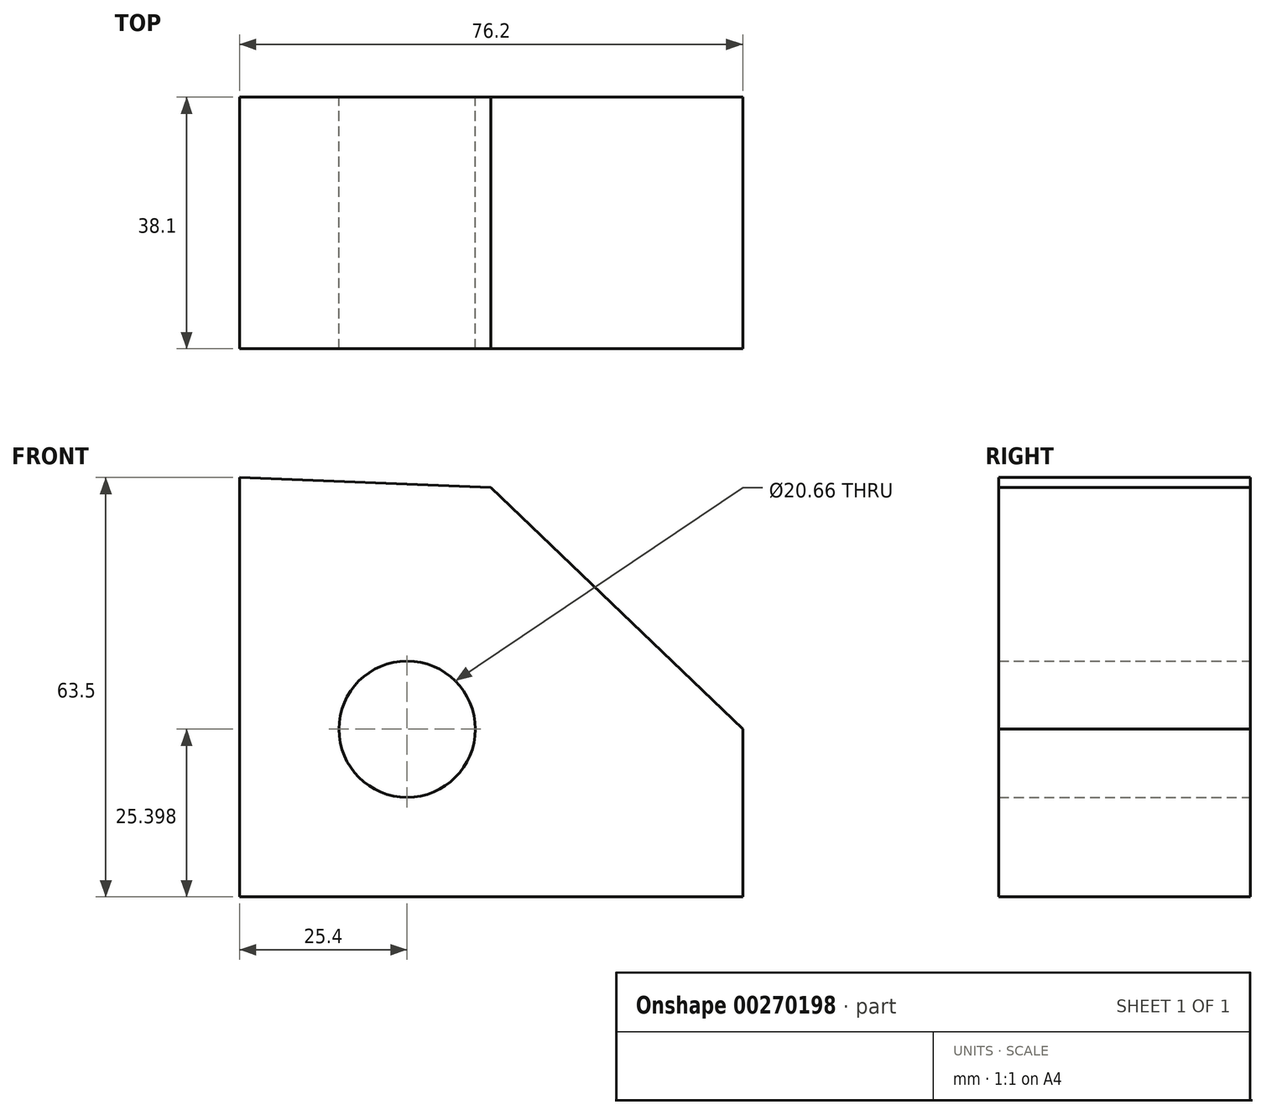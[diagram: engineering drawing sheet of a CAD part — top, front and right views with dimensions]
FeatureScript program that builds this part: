
annotation { "Feature Type Name" : "Feature", "Feature Type Description" : "" }
export const myFeature = defineFeature(function(context is Context, id is Id, definition is map)
    precondition{}
    {
        {
            var Q0;
            Q0=qCreatedBy(makeId("Front.planeOp"),FACE);
            var sketch = newSketch(context, id + "F0", { "sketchPlane" : qUnion([Q0])});
            skLineSegment(sketch, "E0", {"start": v(0, 68.2) * mm, "end": v(0, 4.7) * mm});
            skLineSegment(sketch, "E1", {"start": v(0, 4.7) * mm, "end": v(76.2, 4.7) * mm});
            skLineSegment(sketch, "E2", {"start": v(76.2, 4.7) * mm, "end": v(76.2, 30.1) * mm});
            skLineSegment(sketch, "E3", {"start": v(76.2, 30.1) * mm, "end": v(38.1, 66.72) * mm});
            skLineSegment(sketch, "E4", {"start": v(38.1, 66.72) * mm, "end": v(0, 68.2) * mm});
            skCircle(sketch, "E5", {"center": v(25.4, 30.1) * mm, "radius": 10.33 * mm});
            skSolve(sketch);
        }
        {
            var Q0;
            Q0=makeQuery(id+"F0.imprint","IMPRINT",FACE,{"disambiguationData":[TD([[makeQuery(id+"F0.imprint","IMPRINT",EDGE,{"derivedFrom":sQuery(id+"F0.wireOp",EDGE,"E0")}),1.0]])]});
            extrude(context, id + "F1", {"entities" : qUnion([Q0]), "endBound" : BoundingType.SYMMETRIC, "depth" : 38.1 * mm});
        }
    });
